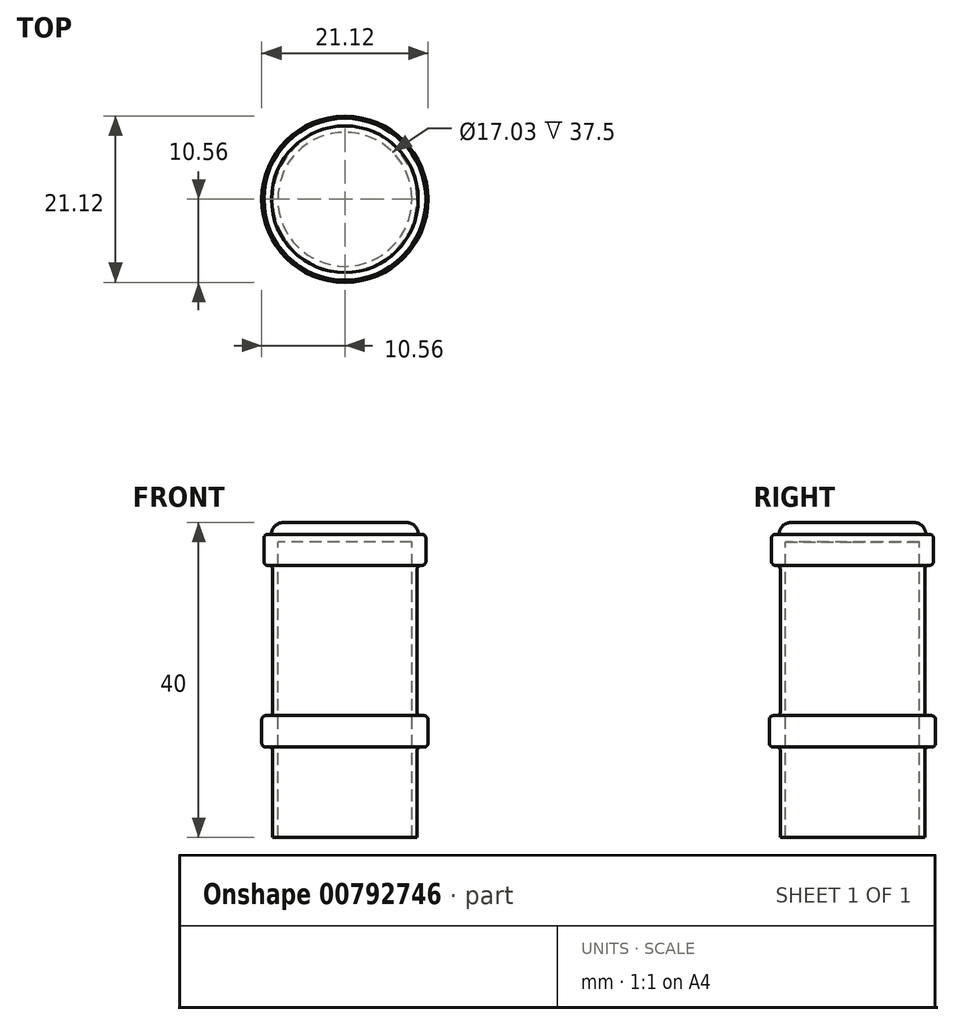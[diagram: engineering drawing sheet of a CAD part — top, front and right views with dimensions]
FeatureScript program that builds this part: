
annotation { "Feature Type Name" : "Feature", "Feature Type Description" : "" }
export const myFeature = defineFeature(function(context is Context, id is Id, definition is map)
    precondition{}
    {
        {
            var Q0;
            Q0=qCreatedBy(makeId("Front.planeOp"),FACE);
            var sketch = newSketch(context, id + "F0", { "sketchPlane" : qUnion([Q0])});
            skLineSegment(sketch, "E0", {"start": v(0, 25.59) * mm, "end": v(8.51, 25.59) * mm});
            skLineSegment(sketch, "E1", {"start": v(8.51, 25.59) * mm, "end": v(8.52, -11.91) * mm});
            skLineSegment(sketch, "E2", {"start": v(0, 28.09) * mm, "end": v(7.82, 28.09) * mm});
            skLineSegment(sketch, "E3", {"start": v(11, 25.01) * mm, "end": v(11, 25) * mm});
            skLineSegment(sketch, "E4", {"start": v(9.18, 22.14) * mm, "end": v(9.18, 3.95) * mm});
            skLineSegment(sketch, "E5", {"start": v(9.57, 3.56) * mm, "end": v(10.06, 3.56) * mm});
            skLineSegment(sketch, "E6", {"start": v(10.56, 3.06) * mm, "end": v(10.56, 0.06) * mm});
            skLineSegment(sketch, "E7", {"start": v(10.06, -0.44) * mm, "end": v(9.57, -0.44) * mm});
            skLineSegment(sketch, "E8", {"start": v(9.18, -0.84) * mm, "end": v(9.18, -11.91) * mm});
            skPoint(sketch, "E9.visualSharp", {"position": v(11, 28.5) * mm});
            skPoint(sketch, "E10.visualSharp", {"position": v(9.32, 28.09) * mm});
            skArc(sketch, "E10.filletArc", {"start": v(9.32, 26.59) * mm, "mid": v(8.88, 27.65) * mm, "end": v(7.82, 28.09) * mm});
            skArc(sketch, "E11.filletArc", {"start": v(9.18, 3.95) * mm, "mid": v(9.3, 3.67) * mm, "end": v(9.57, 3.56) * mm});
            skArc(sketch, "E12.filletArc", {"start": v(10.56, 3.06) * mm, "mid": v(10.4, 3.4) * mm, "end": v(10.06, 3.56) * mm});
            skArc(sketch, "E13.filletArc", {"start": v(10.06, -0.44) * mm, "mid": v(10.4, -0.3) * mm, "end": v(10.56, 0.06) * mm});
            skArc(sketch, "E14.filletArc", {"start": v(9.57, -0.44) * mm, "mid": v(9.3, -0.56) * mm, "end": v(9.18, -0.84) * mm});
            skLineSegment(sketch, "E15", {"start": v(9.32, 26.59) * mm, "end": v(9.79, 26.59) * mm});
            skLineSegment(sketch, "E16", {"start": v(10.29, 26.09) * mm, "end": v(10.29, 23.14) * mm});
            skLineSegment(sketch, "E17", {"start": v(9.79, 22.64) * mm, "end": v(9.68, 22.64) * mm});
            skPoint(sketch, "E18.visualSharp", {"position": v(10.29, 26.59) * mm});
            skArc(sketch, "E18.filletArc", {"start": v(10.29, 26.09) * mm, "mid": v(10.14, 26.44) * mm, "end": v(9.79, 26.59) * mm});
            skPoint(sketch, "E19.visualSharp", {"position": v(9.18, 22.64) * mm});
            skArc(sketch, "E19.filletArc", {"start": v(9.68, 22.64) * mm, "mid": v(9.32, 22.5) * mm, "end": v(9.18, 22.14) * mm});
            skPoint(sketch, "E20.visualSharp", {"position": v(10.29, 22.64) * mm});
            skArc(sketch, "E20.filletArc", {"start": v(9.79, 22.64) * mm, "mid": v(10.14, 22.8) * mm, "end": v(10.29, 23.14) * mm});
            skLineSegment(sketch, "E21", {"start": v(8.52, -11.91) * mm, "end": v(9.18, -11.91) * mm});
            skLineSegment(sketch, "E22", {"start": v(0, 28.09) * mm, "end": v(0, 25.59) * mm});
            skLineSegment(sketch, "E23", {"start": v(0, 28.09) * mm, "end": v(0, -10.52) * mm, "construction": true});
            skSolve(sketch);
        }
        {
            var Q0;
            Q0=makeQuery(id+"F0.imprint","IMPRINT",FACE,{"disambiguationData":[TD([[makeQuery(id+"F0.imprint","IMPRINT",EDGE,{"derivedFrom":sQuery(id+"F0.wireOp",EDGE,"E0")}),1.0]])]});
            var Q1;
            Q1=sQuery(id+"F0.wireOp",EDGE,"E23");
            revolve(context, id + "F1", {"surfaceOperationType" : NewSurfaceOperationType.NEW, "entities" : qUnion([Q0]), "axis" : qUnion([Q1]), "revolveType" : RevolveType.FULL});
        }
    });
